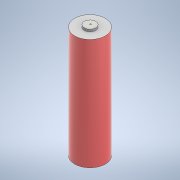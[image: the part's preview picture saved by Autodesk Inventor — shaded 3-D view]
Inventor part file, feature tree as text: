
AUTODESK INVENTOR PART (.ipt)
format: ipt  version: 2020 (Build 240168000, 168)  size: 109,056 bytes
history: native  units: mm
features: sketch x3, other x2, extrude x2
ambient origin geometry x8: Origin, YZ Plane, XZ Plane, XY Plane, X Axis, Y Axis, Z Axis, Center Point
bodies: Body1 (feature_tree)
feature tree (7):
  other  "Sólido1"
  extrude  "Extrusión1"  Depth=52.4mm TaperAngle=0.0deg
  extrude  "Extrusión2"  Depth=1.0mm TaperAngle=0.0deg
  sketch  "Boceto3"
  other  "Eje de trabajo1"
  sketch  "Boceto1"  dims[d0=14.4mm d1=52.4mm d2=0.0mm]
  sketch  "Boceto2"  dims[d3=5.4mm d4=1.0mm d5=0.0mm]
